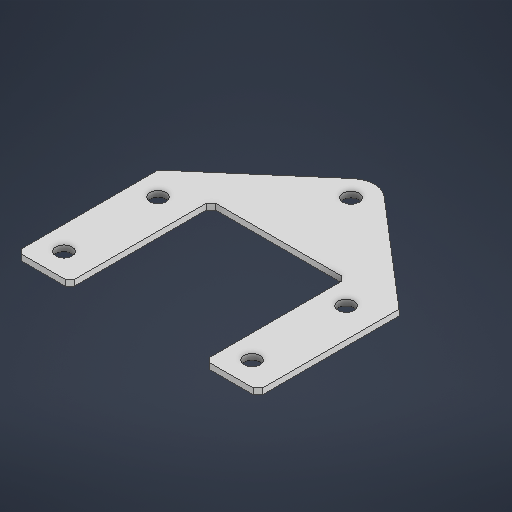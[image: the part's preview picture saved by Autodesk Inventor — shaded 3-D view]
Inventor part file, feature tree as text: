
AUTODESK INVENTOR PART (.ipt)
format: ipt  version: 2025.2 (Build 292293000, 293)  size: 225,280 bytes
history: native  units: in
note: dims shown in document units (in); Inventor stores cm internally (conversion verified against a paired STEP export)
features: extrude x1, sketch x1
ambient origin geometry x8: Origin, YZ Plane, XZ Plane, XY Plane, X Axis, Y Axis, Z Axis, Center Point
bodies: Solid1 (feature_tree)
feature tree (2):
  extrude  "Extrusion1"  Depth=0.0625in TaperAngle=0.0deg
  sketch  "Sketch1"  dims[d0=0.25in d1=0.05in d2=0.05in d3=1.5in d4=0.05in d5=0.05in d6=0.05in d7=0.05in d8=1.5in d9=0.05in d10=0.05in d11=0.05in d12=0.05in d13=0.05in d14=0.05in d16=0.0625in d17=0.0in d19=0.04in d20=1.45in d26=0.25in d27=0.172in]
